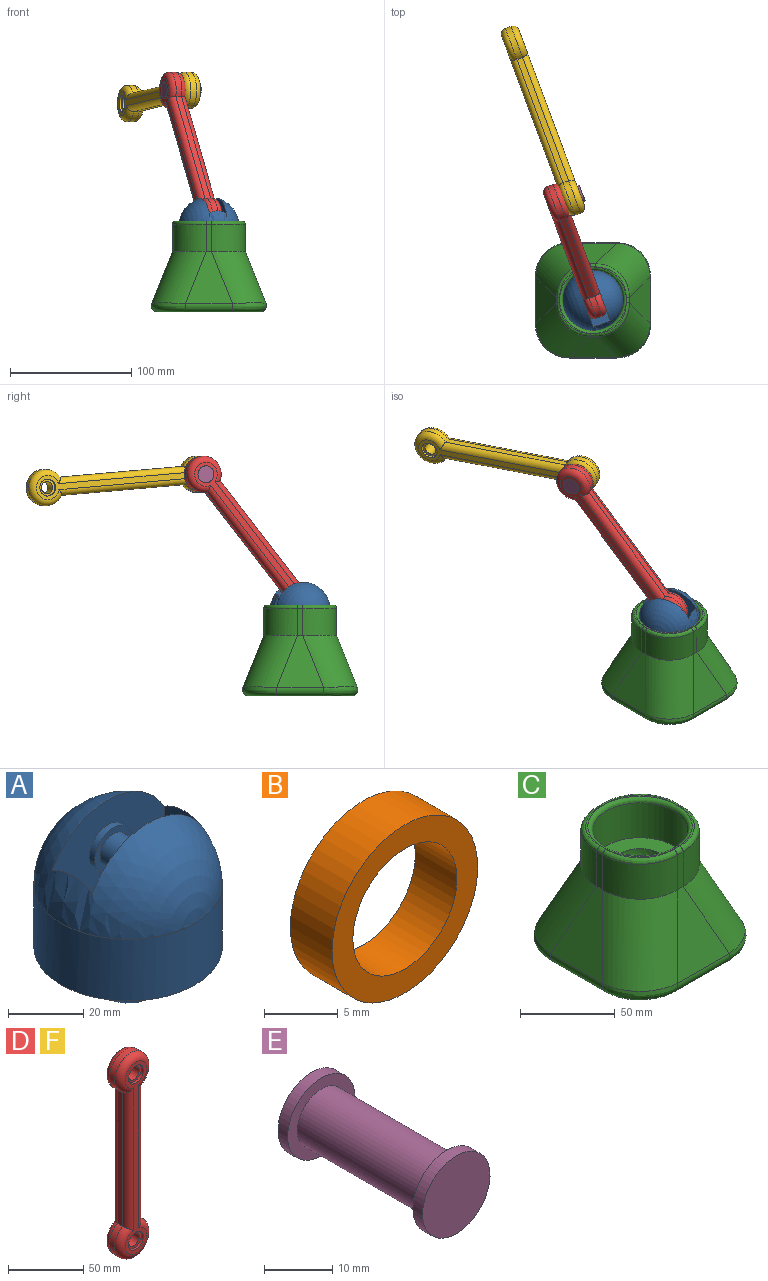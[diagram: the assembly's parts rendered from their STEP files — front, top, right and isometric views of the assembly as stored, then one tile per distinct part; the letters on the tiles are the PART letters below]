
ASSEMBLY  parts=6 mates=6
PART A: 14 faces, bbox 50x50x60 mm
  f0: sphere r=25mm, area 3160.2mm2, adj f1,f4,f5,f6,f7
  f1: cylinder r=25mm len=50mm, axis (0,0,1), area 3141.6mm2, adj f0,f2
  f2: plane 50x50mm, normal (0,0,-1), area 1256.6mm2, adj f1,f3
  f3: sphere r=15mm, area 1413.7mm2, adj f2
  f4: plane 28.56x15mm, normal (-1,0,0), area 417.6mm2, adj f0,f5,f7,f8
  f5: plane 42x38.85mm, normal (0,1,0), area 1326mm2, adj f0,f4,f6,f8,f9
  f6: plane 28.56x15mm, normal (1,0,0), area 417.6mm2, adj f0,f5,f7,f8
  f7: plane 42x38.85mm, normal (0,-1,0), area 1326mm2, adj f0,f4,f6,f8,f12
  f8: plane 42x15mm, normal (0,0,1), area 630mm2, adj f4,f5,f6,f7
  f9: cylinder r=7mm len=14mm, axis (0,-1,0), area 88mm2, adj f5,f10
  f10: plane 14x14mm, normal (0,1,0), area 75.4mm2, adj f9,f11
  f11: cylinder r=5mm len=11mm, axis (0,-1,0), area 345.6mm2, adj f10,f13
  f12: cylinder r=7mm len=14mm, axis (0,1,0), area 88mm2, adj f7,f13
  f13: plane 14x14mm, normal (0,-1,0), area 75.4mm2, adj f11,f12
PART B: 4 faces, bbox 14x4x14 mm
  f0: cylinder r=5mm len=10mm, axis (0,-1,0), area 125.7mm2, adj f2,f3
  f1: cylinder r=7mm len=14mm, axis (0,-1,0), area 175.9mm2, adj f2,f3
  f2: plane 14x14mm, normal (0,1,0), area 75.4mm2, adj f0,f1
  f3: plane 14x14mm, normal (0,-1,0), area 75.4mm2, adj f0,f1
PART C: 41 faces, bbox 100.2x100.2x75 mm
  f0: plane 27.5x27.5mm, normal (0,0,1), area 30.8mm2, adj f32,f33,f34,f35
  f1: plane 27.5x27.5mm, normal (0,0,1), area 30.8mm2, adj f32,f34,f36,f38
  f2: plane 27.5x27.5mm, normal (0,0,1), area 30.8mm2, adj f32,f38,f39,f40
  f3: plane 85.23x85.23mm, normal (0,0,-1), area 6821.3mm2, adj f8,f9,f10,f11,f13,f15,f17,f19
  f4: plane 43.14x38.81mm, normal (0,-0.93,0.37), area 1001.3mm2, adj f10,f14,f18,f21
  f5: plane 43.14x38.81mm, normal (0.93,0,0.37), area 1001.3mm2, adj f8,f16,f18,f23
  f6: plane 43.14x38.81mm, normal (0,0.93,0.37), area 1001.3mm2, adj f9,f12,f16,f25
  f7: plane 43.14x38.81mm, normal (-0.93,0,0.37), area 1001.3mm2, adj f11,f12,f14,f28
  f8: cylinder r=5mm len=38.81mm, axis (0,-1,0), area 378.6mm2, adj f3,f5,f17,f19
  f9: cylinder r=5mm len=38.81mm, axis (-1,0,0), area 378.6mm2, adj f3,f6,f13,f17
  f10: cylinder r=5mm len=38.81mm, axis (-1,0,0), area 378.6mm2, adj f3,f4,f15,f19
  f11: cylinder r=5mm len=38.81mm, axis (0,-1,0), area 378.6mm2, adj f3,f7,f13,f15
  f12: cylinder r=30mm len=49.81mm, axis (0.35,-0.35,0.87), area 2110.3mm2, adj f6,f7,f13,f26
  f13: bspline ~34.54x34.54mm, area 430.9mm2, adj f3,f9,f11,f12
  f14: cylinder r=30mm len=49.81mm, axis (-0.35,-0.35,-0.87), area 2110.3mm2, adj f4,f7,f15,f20
  f15: bspline ~28.22x28.22mm, area 430.9mm2, adj f3,f10,f11,f14
  f16: cylinder r=30mm len=49.81mm, axis (0.35,0.35,-0.87), area 2110.3mm2, adj f5,f6,f17,f24
  f17: bspline ~28.22x28.22mm, area 430.9mm2, adj f3,f8,f9,f16
  f18: cylinder r=30mm len=49.81mm, axis (-0.35,0.35,0.87), area 2110.3mm2, adj f4,f5,f19,f22
  f19: bspline ~34.54x34.54mm, area 430.9mm2, adj f3,f8,f10,f18
  f20: extruded ~27.85x27.85mm, area 990.3mm2, adj f14,f21,f28,f37
  f21: plane 22.5x4.29mm, normal (0,-1,0), area 96.6mm2, adj f4,f20,f22,f35
  f22: extruded ~27.85x27.85mm, area 990.3mm2, adj f18,f21,f23,f33
  f23: plane 22.5x4.29mm, normal (1,0,0), area 96.6mm2, adj f5,f22,f24,f34
  f24: extruded ~27.85x27.85mm, area 990.3mm2, adj f16,f23,f25,f36
  f25: plane 22.5x4.29mm, normal (0,1,0), area 96.6mm2, adj f6,f24,f26,f38
  f26: extruded ~27.85x27.85mm, area 990.3mm2, adj f12,f25,f28,f40
  f27: cylinder r=25mm len=50mm, axis (0,0,-1), area 3534.3mm2, adj f31,f32
  f28: plane 22.5x4.29mm, normal (-1,0,0), area 96.6mm2, adj f7,f20,f26,f39
  f29: plane 27.5x27.5mm, normal (0,0,1), area 30.8mm2, adj f32,f35,f37,f39
  f30: sphere r=15mm, area 1413.7mm2, adj f31
  f31: plane 50x50mm, normal (0,0,1), area 1256.6mm2, adj f27,f30
  f32: torus R=27.5mm, axis (0,0,1), area 639.3mm2, adj f0,f1,f2,f27,f29
  f33: bspline ~32.23x32.23mm, area 167.2mm2, adj f0,f22,f34,f35
  f34: cylinder r=2.5mm len=4.29mm, axis (0,-1,0), area 16.9mm2, adj f0,f1,f23,f33,f36
  f35: cylinder r=2.5mm len=4.29mm, axis (-1,0,0), area 16.9mm2, adj f0,f21,f29,f33,f37
  f36: bspline ~32.23x32.23mm, area 167.2mm2, adj f1,f24,f34,f38
  f37: bspline ~32.23x32.23mm, area 167.2mm2, adj f20,f29,f35,f39
  f38: cylinder r=2.5mm len=4.29mm, axis (1,0,0), area 16.9mm2, adj f1,f2,f25,f36,f40
  f39: cylinder r=2.5mm len=4.29mm, axis (0,1,0), area 16.9mm2, adj f2,f28,f29,f37,f40
  f40: bspline ~32.23x32.23mm, area 167.2mm2, adj f2,f26,f38,f39
PART D: 24 faces, bbox 32.5x15x167.5 mm
  f0: cylinder r=5mm len=11mm, axis (0,-1,0), area 345.6mm2, adj f19,f22
  f1: cylinder r=5mm len=11mm, axis (0,-1,0), area 345.6mm2, adj f17,f20
  f2: plane 109.02x5mm, normal (1,0,0), area 545.1mm2, adj f3,f5,f8,f12
  f3: cylinder r=15mm len=30mm, axis (0,1,0), area 392.7mm2, adj f2,f4,f9,f13
  f4: plane 109.02x5mm, normal (-1,0,0), area 545.1mm2, adj f3,f5,f11,f15
  f5: cylinder r=15mm len=30mm, axis (0,1,0), area 392.7mm2, adj f2,f4,f10,f14
  f6: plane 155x20mm, normal (0,-1,0), area 896.5mm2, adj f12,f13,f14,f15,f16,f18
  f7: plane 155x20mm, normal (0,1,0), area 896.5mm2, adj f8,f9,f10,f11,f21,f23
  f8: cylinder r=5mm len=115.64mm, axis (0,0,1), area 874.1mm2, adj f2,f7,f9,f10
  f9: torus R=10mm, axis (0,-1,0), area 558mm2, adj f3,f7,f8,f11
  f10: torus R=10mm, axis (0,-1,0), area 558mm2, adj f5,f7,f8,f11
  f11: cylinder r=5mm len=115.64mm, axis (0,0,-1), area 874.1mm2, adj f4,f7,f9,f10
  f12: cylinder r=5mm len=115.64mm, axis (0,0,-1), area 874.1mm2, adj f2,f6,f13,f14
  f13: torus R=10mm, axis (0,-1,0), area 558mm2, adj f3,f6,f12,f15
  f14: torus R=10mm, axis (0,-1,0), area 558mm2, adj f5,f6,f12,f15
  f15: cylinder r=5mm len=115.64mm, axis (0,0,1), area 874.1mm2, adj f4,f6,f13,f14
  f16: cylinder r=7mm len=14mm, axis (0,-1,0), area 88mm2, adj f6,f17
  f17: plane 14x14mm, normal (0,-1,0), area 75.4mm2, adj f1,f16
  f18: cylinder r=7mm len=14mm, axis (0,-1,0), area 88mm2, adj f6,f19
  f19: plane 14x14mm, normal (0,-1,0), area 75.4mm2, adj f0,f18
  f20: plane 14x14mm, normal (0,1,0), area 75.4mm2, adj f1,f21
  f21: cylinder r=7mm len=14mm, axis (0,1,0), area 88mm2, adj f7,f20
  f22: plane 14x14mm, normal (0,1,0), area 75.4mm2, adj f0,f23
  f23: cylinder r=7mm len=14mm, axis (0,1,0), area 88mm2, adj f7,f22
PART E: 7 faces, bbox 14x30x14 mm
  f0: plane 14x14mm, normal (0,1,0), area 75.4mm2, adj f1,f6
  f1: cylinder r=5mm len=26mm, axis (0,1,0), area 816.8mm2, adj f0,f2
  f2: plane 14x14mm, normal (0,-1,0), area 75.4mm2, adj f1,f3
  f3: cylinder r=7mm len=14mm, axis (0,1,0), area 88mm2, adj f2,f4
  f4: plane 14x14mm, normal (0,1,0), area 153.9mm2, adj f3
  f5: plane 14x14mm, normal (0,-1,0), area 153.9mm2, adj f6
  f6: cylinder r=7mm len=14mm, axis (0,1,0), area 88mm2, adj f0,f5
PART F: same geometry as D
PLACE A rot(axis=(0,0,1),110.4deg) t=(57.56,181.95,83.3)mm
PLACE B rot(axis=(-0.17,0.12,0.98),111.6deg) t=(169.2,-123.69,301.61)mm
PLACE C t=(-0.46,12.47,13.3)mm fixed
PLACE D rot(axis=(-0.3,-0.44,-0.85),78.7deg) t=(18.45,167.38,1.76)mm
PLACE E rot(axis=(-0.33,0.23,0.92),115.1deg) t=(139.68,-32.78,366.59)mm
PLACE F rot(axis=(-0.65,0.45,0.6),134.5deg) t=(20.79,155.37,337.6)mm
MATE revolute F.f0 <-> E.f1  axis (-0.94,-0.35,0) through (26.59,145.55,196.32)mm
MATE ball A.f1 <-> C.f27  axis (0,0,-1) through (49.54,62.47,63.3)mm
MATE planar A.f1 <-> C.f27  axis (0,0,-1) through (49.54,62.47,63.3)mm
MATE revolute D.f0 <-> A.f9  axis (-0.94,-0.35,0) through (44.39,60.55,92.15)mm
MATE fastened E.f1 <-> D.f1  axis (0.94,0.35,0) through (14.41,141.01,196.32)mm
MATE revolute B.f0 <-> D.f1  axis (-0.94,-0.35,0) through (24.71,144.85,196.32)mm
